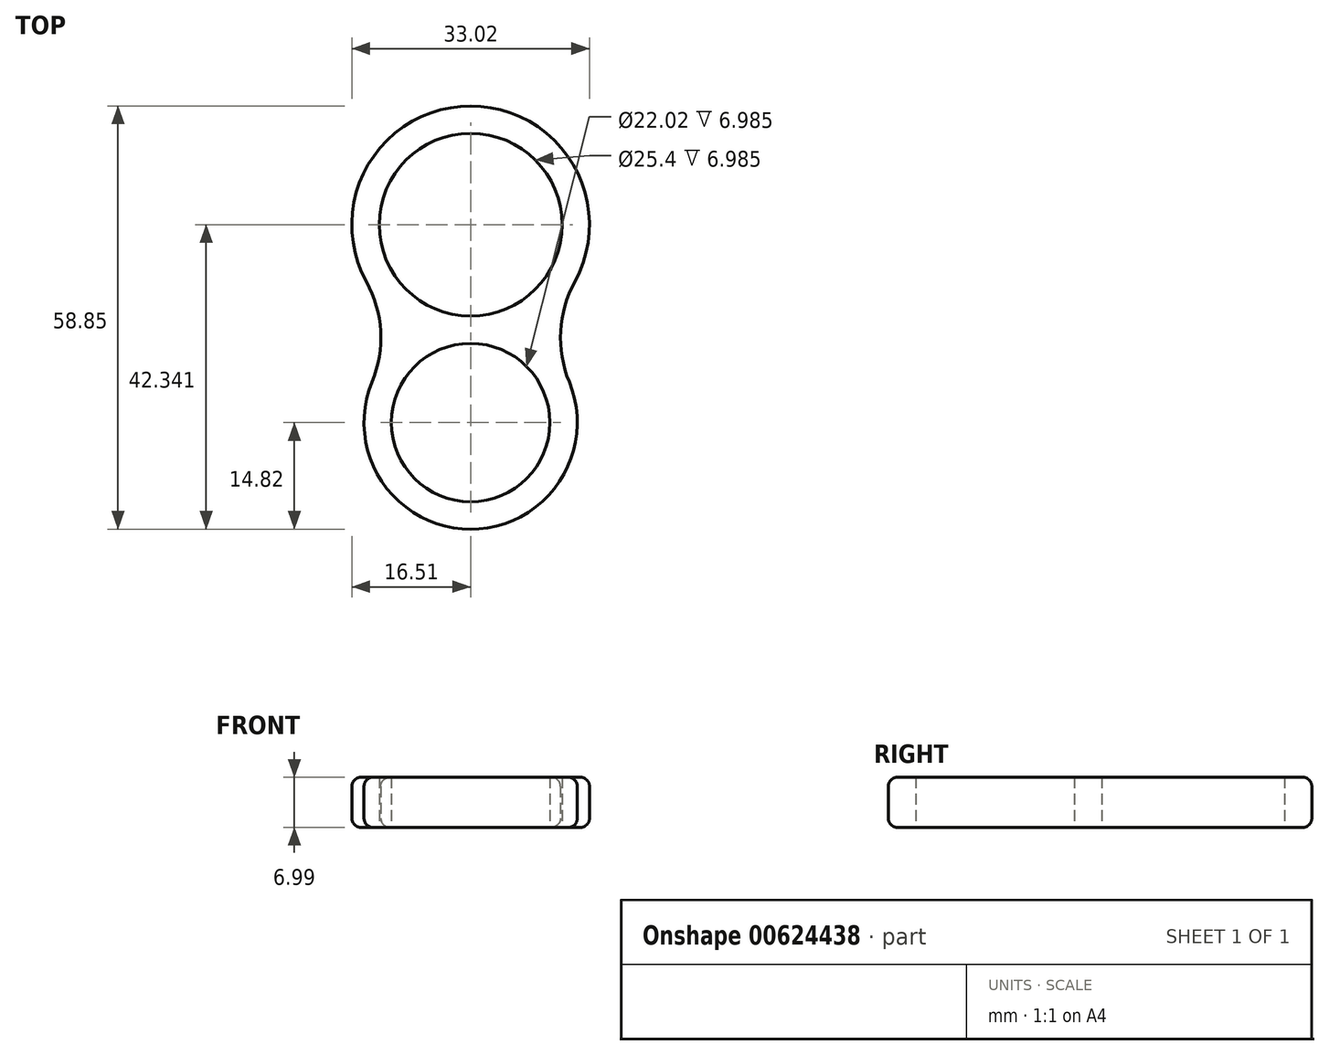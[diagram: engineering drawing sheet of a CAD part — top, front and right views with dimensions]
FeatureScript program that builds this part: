
annotation { "Feature Type Name" : "Feature", "Feature Type Description" : "" }
export const myFeature = defineFeature(function(context is Context, id is Id, definition is map)
    precondition{}
    {
        {
            var Q0;
            Q0=qCreatedBy(makeId("Top.planeOp"),FACE);
            var sketch = newSketch(context, id + "F0", { "sketchPlane" : qUnion([Q0])});
            skCircle(sketch, "E0", {"center": v(0, 0) * mm, "radius": 11.01 * mm});
            skLineSegment(sketch, "E1", {"start": v(0, 0) * mm, "end": v(0, 27.52) * mm});
            skCircle(sketch, "E2", {"center": v(0, 27.52) * mm, "radius": 12.7 * mm});
            skCircle(sketch, "E3.0", {"center": v(0, 27.52) * mm, "radius": 16.51 * mm});
            skCircle(sketch, "E4.0", {"center": v(0, 0) * mm, "radius": 14.82 * mm});
            skArc(sketch, "E5", {"start": v(-13.7, 5.64) * mm, "mid": v(-12.51, 12.7) * mm, "end": v(-14.48, 19.59) * mm});
            skArc(sketch, "E6", {"start": v(14.48, 19.58) * mm, "mid": v(12.5, 12.7) * mm, "end": v(13.7, 5.64) * mm});
            skSolve(sketch);
        }
        {
            var Q0;
            {var subQ0=sQuery(id+"F0.wireOp",EDGE,"E5");Q0=makeQuery(id+"F0.imprint","IMPRINT",FACE,{"disambiguationData":[TD([[makeQuery(id+"F0.imprint","IMPRINT",EDGE,{"derivedFrom":subQ0}),-1.0]])]});}
            var Q1;
            {var subQ0=sQuery(id+"F0.wireOp",EDGE,"E6");Q1=makeQuery(id+"F0.imprint","IMPRINT",FACE,{"disambiguationData":[TD([[makeQuery(id+"F0.imprint","IMPRINT",EDGE,{"derivedFrom":subQ0}),-1.0]])]});}
            var Q2;
            {var subQ4=sQuery(id+"F0.wireOp",EDGE,"E0");Q2=makeQuery(id+"F0.imprint","IMPRINT",FACE,{"disambiguationData":[TD([[makeQuery(id+"F0.imprint","IMPRINT",EDGE,{"derivedFrom":subQ4}),-1.0]])]});}
            var Q3;
            {var subQ6=sQuery(id+"F0.wireOp",EDGE,"E2");Q3=makeQuery(id+"F0.imprint","IMPRINT",FACE,{"disambiguationData":[TD([[makeQuery(id+"F0.imprint","IMPRINT",EDGE,{"derivedFrom":subQ6}),-1.0]])]});}
            var Q4;
            {var subQ0=sQuery(id+"F0.wireOp",EDGE,"E3.0");var subQ3=sQuery(id+"F0.wireOp",EDGE,"E4.0");var subQ5=makeQuery(id+"F0.imprint","INTERSECT",VERTEX,{"disambiguationData":[OD(1.0)],"derivedFrom":[subQ0,subQ3]});Q4=makeQuery(id+"F0.imprint","IMPRINT",FACE,{"disambiguationData":[TD([[makeQuery(id+"F0.imprint","IMPRINT",EDGE,{"disambiguationData":[TD([[subQ5,1.0]])],"derivedFrom":subQ0}),1.0]])]});}
            var Q5;
            {var subQ0=sQuery(id+"F0.wireOp",EDGE,"E3.0");var subQ3=sQuery(id+"F0.wireOp",EDGE,"E4.0");var subQ5=makeQuery(id+"F0.imprint","INTERSECT",VERTEX,{"disambiguationData":[OD(0.0)],"derivedFrom":[subQ0,subQ3]});Q5=makeQuery(id+"F0.imprint","IMPRINT",FACE,{"disambiguationData":[TD([[makeQuery(id+"F0.imprint","IMPRINT",EDGE,{"disambiguationData":[TD([[subQ5,-1.0]])],"derivedFrom":subQ0}),1.0]])]});}
            extrude(context, id + "F1", {"entities" : qUnion([Q0, Q1, Q2, Q3, Q4, Q5]), "depth" : 7 * mm, "offsetDistance" : 25.4 * mm});
        }
        {
            var Q0;
            Q0=makeQuery(id+"F1.opExtrude","CAP_EDGE",EDGE,{"disambiguationData":[OSD([sQuery(id+"F0.wireOp",EDGE,"E3.0")])],"isStart":false});
            var Q1;
            Q1=makeQuery(id+"F1.opExtrude","CAP_EDGE",EDGE,{"disambiguationData":[OSD([sQuery(id+"F0.wireOp",EDGE,"E3.0")])],"isStart":true});
            fillet(context, id + "F2", {"entities" : qUnion([Q0, Q1]), "radius" : 1.27 * mm, "tangentPropagation" : true, "allowEdgeOverflow" : false});
        }
    });
